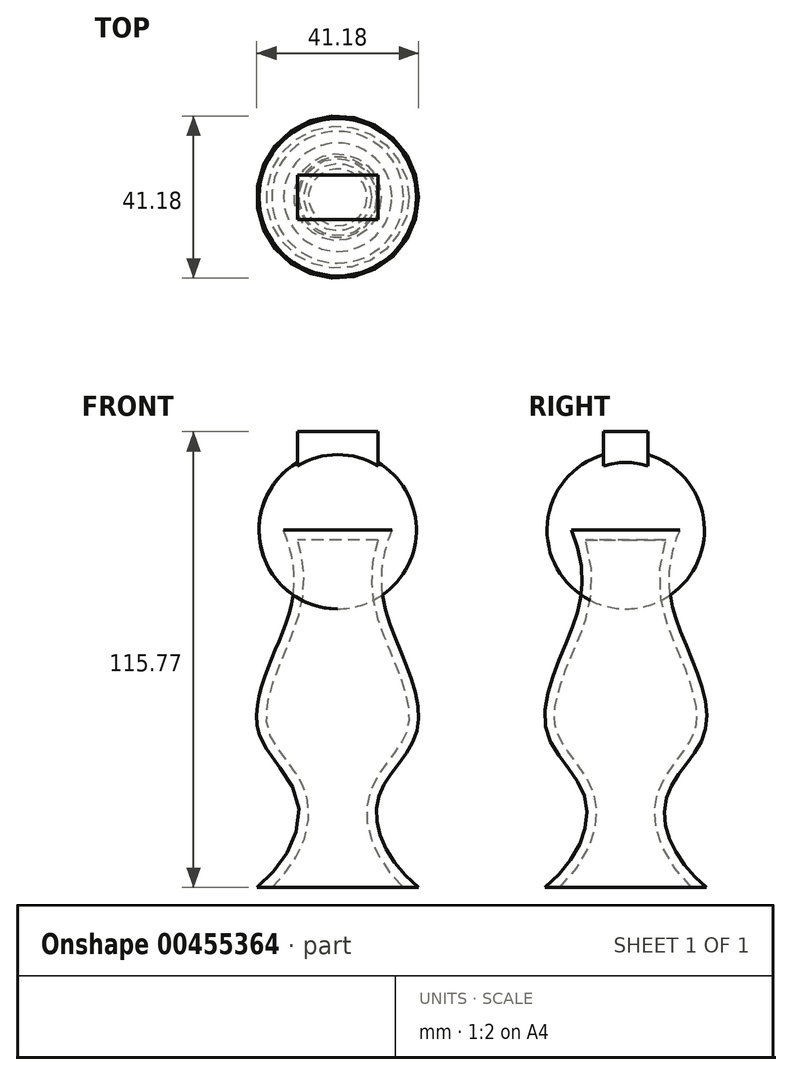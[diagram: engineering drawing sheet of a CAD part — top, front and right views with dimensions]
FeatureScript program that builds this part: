
annotation { "Feature Type Name" : "Feature", "Feature Type Description" : "" }
export const myFeature = defineFeature(function(context is Context, id is Id, definition is map)
    precondition{}
    {
        {
            var Q0;
            Q0=qCreatedBy(makeId("Front.planeOp"),FACE);
            var sketch = newSketch(context, id + "F0", { "sketchPlane" : qUnion([Q0])});
            skArc(sketch, "E0", {"start": v(0, -20) * mm, "mid": v(20, 0) * mm, "end": v(0, 20) * mm});
            skLineSegment(sketch, "E1", {"start": v(0, 32.3) * mm, "end": v(0, -32.8) * mm, "construction": true});
            skLineSegment(sketch, "E2", {"start": v(-59.46, 0) * mm, "end": v(60.37, 0) * mm, "construction": true});
            skLineSegment(sketch, "E3", {"start": v(0, 20) * mm, "end": v(0, -20) * mm});
            skSolve(sketch);
        }
        {
            var Q0;
            Q0=makeQuery(id+"F0.imprint","IMPRINT",FACE,{"disambiguationData":[TD([[makeQuery(id+"F0.imprint","IMPRINT",EDGE,{"derivedFrom":sQuery(id+"F0.wireOp",EDGE,"E0")}),1.0]])]});
            var Q1;
            Q1=sQuery(id+"F0.wireOp",EDGE,"E3");
            revolve(context, id + "F1", {"entities" : qUnion([Q0]), "axis" : qUnion([Q1]), "revolveType" : RevolveType.FULL});
        }
        {
            var Q0;
            Q0=qCreatedBy(makeId("Top.planeOp"),FACE);
            var sketch = newSketch(context, id + "F2", { "sketchPlane" : qUnion([Q0])});
            skLineSegment(sketch, "E4.bottom", {"start": v(10.23, 5.66) * mm, "end": v(-10.23, 5.66) * mm});
            skLineSegment(sketch, "E4.top", {"start": v(10.23, -5.66) * mm, "end": v(-10.23, -5.66) * mm});
            skLineSegment(sketch, "E4.left", {"start": v(10.23, 5.66) * mm, "end": v(10.23, -5.66) * mm});
            skLineSegment(sketch, "E4.right", {"start": v(-10.23, 5.66) * mm, "end": v(-10.23, -5.66) * mm});
            skPoint(sketch, "E4.middle", {"position": v(0, 0) * mm});
            skSolve(sketch);
        }
        {
            var Q0;
            Q0 = qSketchRegion(id + "F2", true);
            extrude(context, id + "F3", {"entities" : qUnion([Q0]), "operationType" : NewBodyOperationType.ADD, "depth" : 25 * mm});
        }
        {
            var Q0;
            Q0=qCreatedBy(makeId("Front.planeOp"),FACE);
            var sketch = newSketch(context, id + "F4", { "sketchPlane" : qUnion([Q0])});
            skFitSpline(sketch, "E5", {"points": [v(-13.75, 0) * mm, v(-16.06, -30.87) * mm, v(-19.92, -51.9) * mm, v(-10.3, -68.19) * mm, v(-20.53, -90.77) * mm], "startDerivative": vector(58.31, -142.55) * mm, "endDerivative": vector(-97.05, -78.49) * mm});
            skLineSegment(sketch, "E6", {"start": v(-13.75, 0) * mm, "end": v(0, 0) * mm});
            skLineSegment(sketch, "E7", {"start": v(0, 0) * mm, "end": v(0, -90.77) * mm});
            skLineSegment(sketch, "E8", {"start": v(0, -90.77) * mm, "end": v(-20.53, -90.77) * mm});
            skSolve(sketch);
        }
        {
            var Q0;
            Q0=makeQuery(id+"F4.imprint","IMPRINT",FACE,{"disambiguationData":[TD([[makeQuery(id+"F4.imprint","IMPRINT",EDGE,{"derivedFrom":sQuery(id+"F4.wireOp",EDGE,"E5")}),1.0]])]});
            var Q1;
            Q1=sQuery(id+"F4.wireOp",EDGE,"E7");
            revolve(context, id + "F5", {"entities" : qUnion([Q0]), "axis" : qUnion([Q1]), "revolveType" : RevolveType.FULL});
        }
        {
            var Q0;
            Q0=qCreatedBy(makeId("Front.planeOp"),FACE);
            var sketch = newSketch(context, id + "F6", { "sketchPlane" : qUnion([Q0])});
            skCircle(sketch, "E9", {"center": v(0, 0) * mm, "radius": 8 * mm});
            skSolve(sketch);
        }
        {
            var Q0;
            Q0=qCreatedBy(makeId("Front.planeOp"),FACE);
            cPlane(context, id + "F7", {"entities" : qUnion([Q0]), "cplaneType" : CPlaneType.OFFSET, "offset" : 30 * mm, "width" : 150 * mm, "height" : 150 * mm});
        }
        {
            var Q0;
            Q0=qCreatedBy(id+"F7.planeOp",FACE);
            var sketch = newSketch(context, id + "F8", { "sketchPlane" : qUnion([Q0])});
            skCircle(sketch, "E10", {"center": v(0, 0) * mm, "radius": 3.32 * mm});
            skSolve(sketch);
        }
        {
            var Q0;
            Q0=sQuery(id+"F6.wireOp",EDGE,"E9");
            var Q1;
            Q1=sQuery(id+"F8.wireOp",EDGE,"E10");
            loft(context, id + "F9", {"bodyType" : ToolBodyType.SURFACE, "wireProfilesArray" : [{ "wireProfileEntities" : qUnion([Q0]) }, { "wireProfileEntities" : qUnion([Q1]) }]});
        }
        {
            var Q0;
            Q0=makeQuery(id+"F5.opRevolve","SWEPT_FACE",FACE,{"disambiguationData":[OSD([sQuery(id+"F4.wireOp",EDGE,"E8")])]});
            shell(context, id + "F10", {"entities" : qUnion([Q0]), "thickness" : 2.5 * mm});
        }
    });
